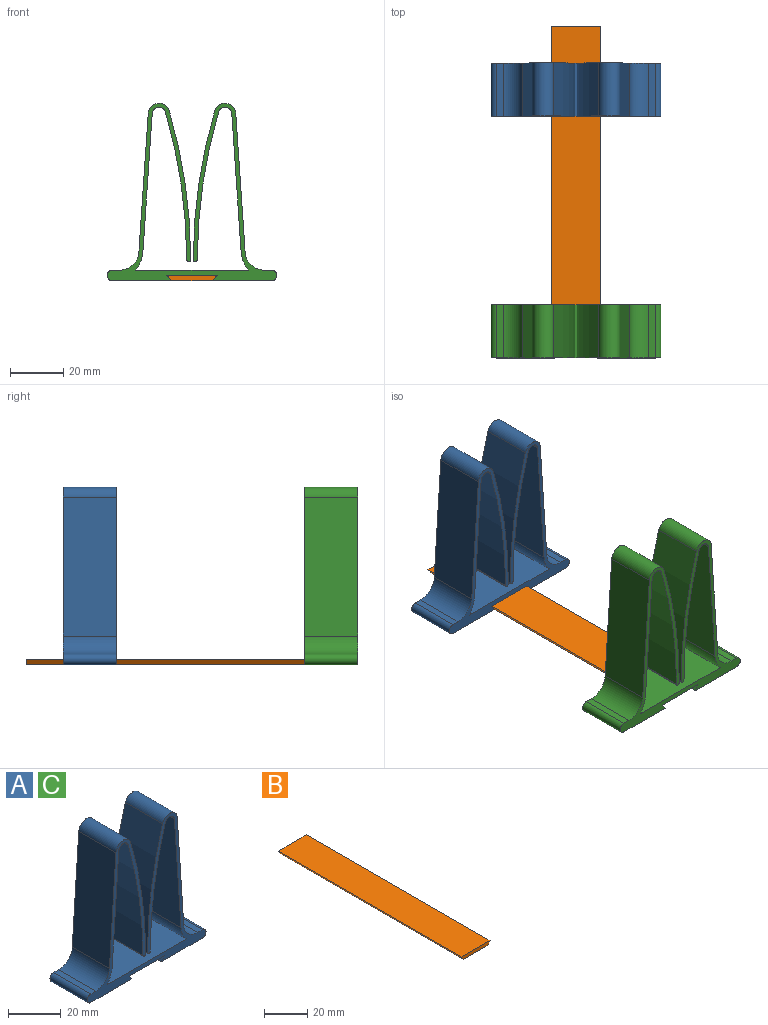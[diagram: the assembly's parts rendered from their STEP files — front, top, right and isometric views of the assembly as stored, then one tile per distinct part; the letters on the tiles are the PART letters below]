
ASSEMBLY  parts=3 mates=2
PART A: 30 faces, bbox 64x20x66.9 mm
  f0: plane 22x20mm, normal (0,0,-1), area 440mm2, adj f1,f13,f14,f15
  f1: plane 66.91x64mm, normal (0,-1,0), area 604.6mm2, adj f0,f2,f3,f4,f5,f6,f7,f8
  f2: plane 42.56x20mm, normal (0,0,1), area 851.3mm2, adj f1,f3,f14,f18
  f3: cylinder r=11.5mm len=20mm, axis (0,1,0), area 148mm2, adj f1,f2,f4,f14
  f4: plane 52.3x20mm, normal (1,0,-0.07), area 1048.3mm2, adj f1,f3,f5,f14
  f5: cylinder r=2.55mm len=20mm, axis (0,1,0), area 142.5mm2, adj f1,f4,f6,f14
  f6: cylinder r=197.77mm len=55.57mm, axis (0,1,0), area 1126.7mm2, adj f1,f5,f7,f14
  f7: cylinder r=0.75mm len=20mm, axis (0,1,0), area 47.1mm2, adj f1,f6,f8,f14
  f8: cylinder r=197.78mm len=56mm, axis (0,1,0), area 1135.4mm2, adj f1,f7,f9,f14
  f9: cylinder r=4.05mm len=20mm, axis (0,1,0), area 226.1mm2, adj f1,f8,f10,f14
  f10: plane 52.3x20mm, normal (-1,0,0.07), area 1048.3mm2, adj f1,f9,f11,f14
  f11: cylinder r=7.32mm len=20mm, axis (0,1,0), area 220.2mm2, adj f1,f10,f12,f14
  f12: plane 20x2.67mm, normal (0,0,1), area 53.5mm2, adj f1,f11,f13,f14
  f13: cylinder r=2mm len=20mm, axis (0,1,0), area 125.7mm2, adj f0,f1,f12,f14
  f14: plane 66.91x64mm, normal (0,1,0), area 604.6mm2, adj f0,f2,f3,f4,f5,f6,f7,f8
  f15: plane 20x2.05mm, normal (0.82,0,0.57), area 50.1mm2, adj f0,f1,f14,f16
  f16: plane 20x18.87mm, normal (0,0,-1), area 377.4mm2, adj f1,f14,f15,f29
  f17: plane 22x20mm, normal (0,0,-1), area 440mm2, adj f1,f14,f28,f29
  f18: cylinder r=11.5mm len=20mm, axis (0,1,0), area 148mm2, adj f1,f2,f14,f19
  f19: plane 52.3x20mm, normal (-1,0,-0.07), area 1048.3mm2, adj f1,f14,f18,f20
  f20: cylinder r=2.55mm len=20mm, axis (0,1,0), area 142.5mm2, adj f1,f14,f19,f21
  f21: cylinder r=197.77mm len=55.57mm, axis (0,1,0), area 1126.7mm2, adj f1,f14,f20,f22
  f22: cylinder r=0.75mm len=20mm, axis (0,1,0), area 47.1mm2, adj f1,f14,f21,f23
  f23: cylinder r=197.78mm len=56mm, axis (0,1,0), area 1135.4mm2, adj f1,f14,f22,f24
  f24: cylinder r=4.05mm len=20mm, axis (0,1,0), area 226.1mm2, adj f1,f14,f23,f25
  f25: plane 52.3x20mm, normal (1,0,0.07), area 1048.3mm2, adj f1,f14,f24,f26
  f26: cylinder r=7.32mm len=20mm, axis (0,1,0), area 220.2mm2, adj f1,f14,f25,f27
  f27: plane 20x2.67mm, normal (0,0,1), area 53.5mm2, adj f1,f14,f26,f28
  f28: cylinder r=2mm len=20mm, axis (0,1,0), area 125.7mm2, adj f1,f14,f17,f27
  f29: plane 20x2.05mm, normal (-0.82,0,0.57), area 50.1mm2, adj f1,f14,f16,f17
PART B: 6 faces, bbox 18.7x120x2 mm
  f0: plane 120x18.65mm, normal (0,0,1), area 2238.1mm2, adj f1,f3,f4,f5
  f1: plane 120x2mm, normal (-0.82,0,-0.57), area 293mm2, adj f0,f2,f4,f5
  f2: plane 120x15.85mm, normal (0,0,-1), area 1902mm2, adj f1,f3,f4,f5
  f3: plane 120x2mm, normal (0.82,0,-0.57), area 293mm2, adj f0,f2,f4,f5
  f4: plane 18.65x2mm, normal (0,-1,0), area 34.5mm2, adj f0,f1,f2,f3
  f5: plane 18.65x2mm, normal (0,1,0), area 34.5mm2, adj f0,f1,f2,f3
PART C: same geometry as A
PLACE A t=(0,35.99,-0.05)mm
PLACE B rot(axis=(0,0,1),180deg) t=(0,-60,0)mm
PLACE C t=(0,-55.14,-0.05)mm
MATE slider B.f4 <-> C.f1  axis (0,1,0) through (0,60,2)mm
MATE slider B.f4 <-> A.f1  axis (0,1,0) through (0,60,2)mm
